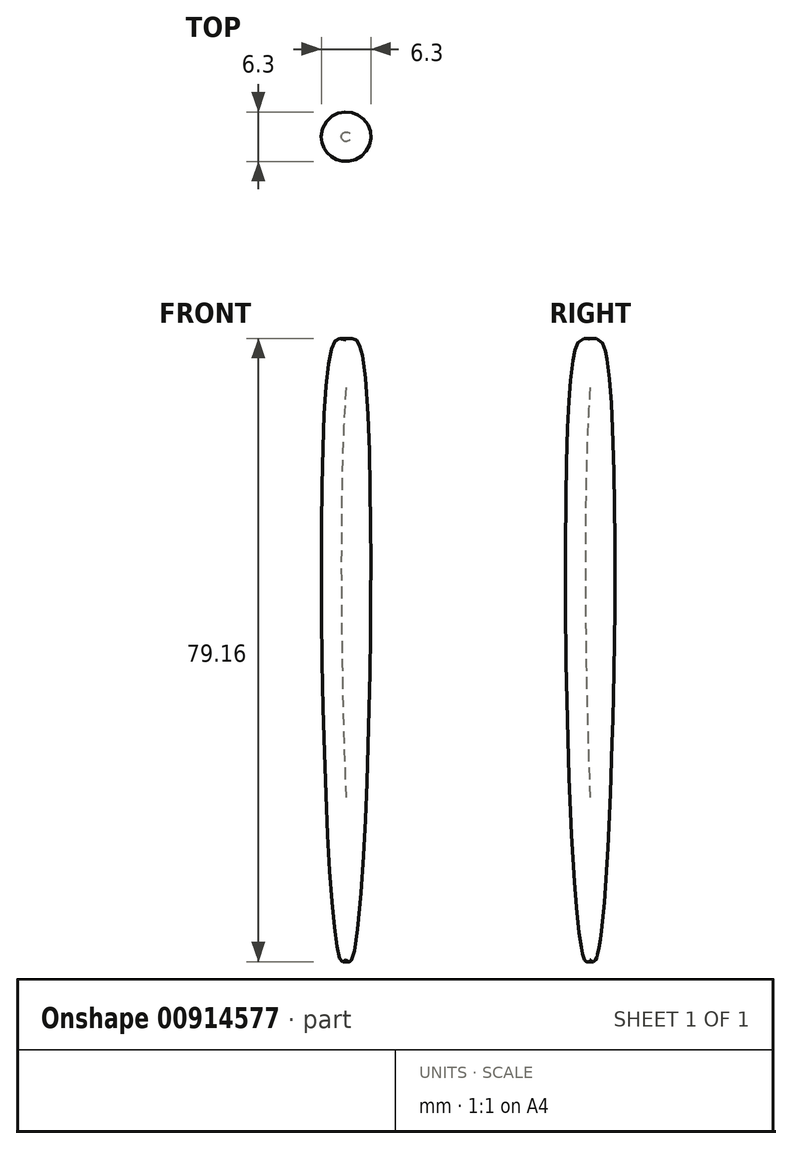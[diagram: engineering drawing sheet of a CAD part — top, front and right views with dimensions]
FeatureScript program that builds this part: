
annotation { "Feature Type Name" : "Feature", "Feature Type Description" : "" }
export const myFeature = defineFeature(function(context is Context, id is Id, definition is map)
    precondition{}
    {
        {
            var Q0;
            Q0=qCreatedBy(makeId("Front.planeOp"),FACE);
            var sketch = newSketch(context, id + "F0", { "sketchPlane" : qUnion([Q0])});
            skLineSegment(sketch, "E0", {"start": v(16.5, 35.36) * mm, "end": v(16.5, -43.4) * mm});
            skFitSpline(sketch, "E1", {"points": [v(16.5, 35.36) * mm, v(14.53, 33.83) * mm, v(15.8, -43.4) * mm, v(16.5, -43.4) * mm], "startDerivative": vector(-21.99, 7.81) * mm, "endDerivative": vector(10.9, 8.4) * mm});
            skLineSegment(sketch, "E2", {"start": v(16.5, 35.36) * mm, "end": v(16.5, -43.4) * mm, "construction": true});
            skSolve(sketch);
        }
        {
            var Q0;
            Q0=makeQuery(id+"F0.imprint","IMPRINT",FACE,{"disambiguationData":[TD([[makeQuery(id+"F0.imprint","IMPRINT",EDGE,{"derivedFrom":sQuery(id+"F0.wireOp",EDGE,"E0")}),-1.0]])]});
            var Q1;
            Q1=sQuery(id+"F0.wireOp",EDGE,"E0");
            revolve(context, id + "F1", {"surfaceOperationType" : NewSurfaceOperationType.NEW, "entities" : qUnion([Q0]), "axis" : qUnion([Q1]), "revolveType" : RevolveType.FULL});
        }
        {
            var Q0;
            Q0=makeQuery(id+"F1.opRevolve","SWEPT_FACE",FACE,{"disambiguationData":[OSD([sQuery(id+"F0.wireOp",EDGE,"E1")])]});
            var Q1;
            Q1=makeQuery(id+"F1.opRevolve","SWEPT_BODY",BODY,{"disambiguationData":[OSD([sQuery(id+"F0.wireOp",EDGE,"E0"),sQuery(id+"F0.wireOp",EDGE,"E1")])]});
            shell(context, id + "F2", {"isHollow" : true, "entities" : qUnion([Q0]), "parts" : qUnion([Q1]), "thickness" : 2.54 * mm});
        }
    });
